# Revit family: TL170DD12
name_source: partatom
category: Generic Models
revit_build: Autodesk Revit LT 2015 (Build: 20140606_1530(x64)
units: mm (PartAtom-declared; Revit-internal decimal feet)

## types (1)
- TL170DD12
    Codes/Standards = • Complies with federal and state lead-free legislation
• Meets or exceeds ASME A112.18.1/CSA B125.1,
NSF 61-9, NSF 372
• Certifications: IAPMO(cUPC), EPA WaterSense,
California Energy Commission (CEC), State of
Massachusetts and others
• Code Compliance: UPC, IPC, NSPC, NPC Canada,
California Green Building Code, City of Los
Angeles Water Efficiency Ordinance, City of New
York and others
    Colors/Finishes = #CP Polished Chrome
    Manufacturer = TOTO USA
    Metal material = Steel, Galvanized
    Model = TL170DD12
    Specifications = • Warranty Lifetime Limited Warranty
(Residential Use)
One Year (Commercial Use)
• Material Brass
• Maximum Flow Rate 1.2 gpm (4.5 lpm)
• Shipping Weight 12.7 lbs.
• Shipping Dimensions 20-1/2"L x 10"W x 3-1/2"H

## geometry (parser evidence)
native form markers: Sweep x2
no freeform markers — native parametric forms only
